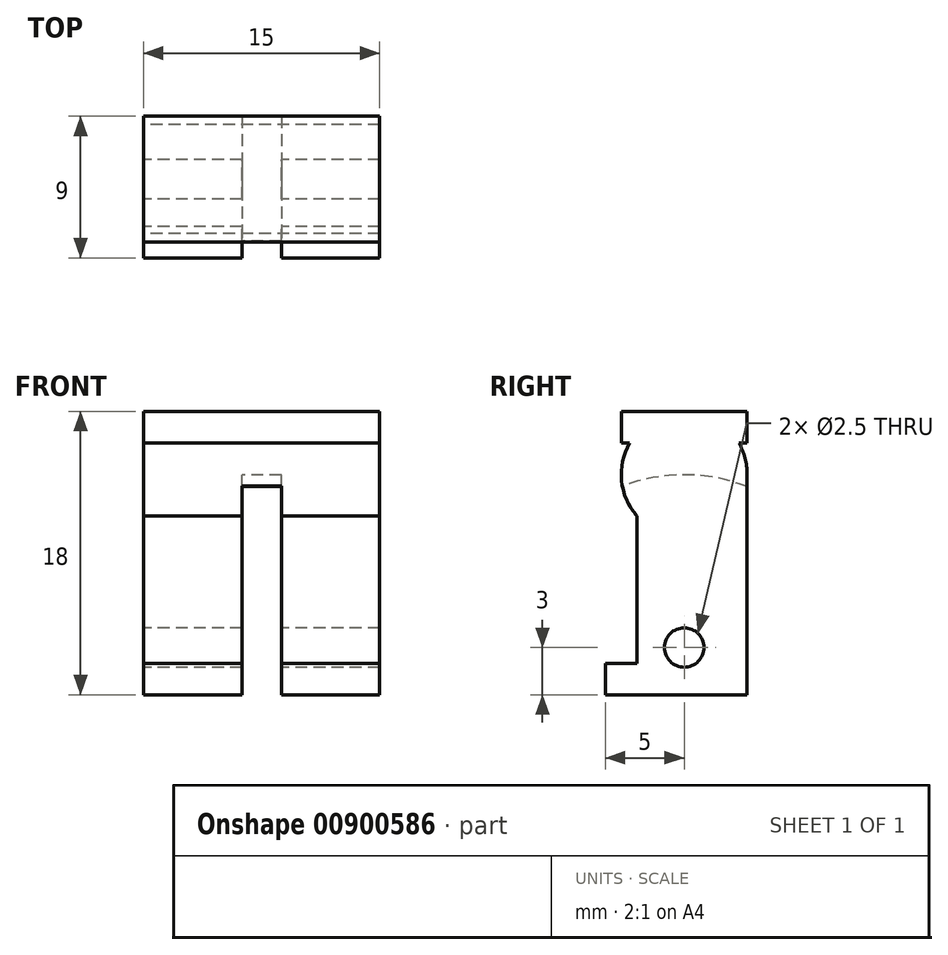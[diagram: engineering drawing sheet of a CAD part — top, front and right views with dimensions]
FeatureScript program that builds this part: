
annotation { "Feature Type Name" : "Feature", "Feature Type Description" : "" }
export const myFeature = defineFeature(function(context is Context, id is Id, definition is map)
    precondition{}
    {
        {
            var Q0;
            Q0=qCreatedBy(makeId("Right.planeOp"),FACE);
            var sketch = newSketch(context, id + "F0", { "sketchPlane" : qUnion([Q0])});
            skLineSegment(sketch, "E0.bottom", {"start": v(4, 1) * mm, "end": v(-4, 1) * mm});
            skLineSegment(sketch, "E0.top", {"start": v(4, -1) * mm, "end": v(3.46, -1) * mm});
            skLineSegment(sketch, "E0.left", {"start": v(4, 1) * mm, "end": v(4, -1) * mm});
            skLineSegment(sketch, "E0.right", {"start": v(-4, 1) * mm, "end": v(-4, -1) * mm});
            skPoint(sketch, "E0.middle", {"position": v(0, 0) * mm});
            skArc(sketch, "E1", {"start": v(-3.46, -1) * mm, "mid": v(-3.98, -3.4) * mm, "end": v(-3, -5.65) * mm});
            skLineSegment(sketch, "E2.left", {"start": v(4, -3) * mm, "end": v(4, -15) * mm});
            skLineSegment(sketch, "E2.right", {"start": v(-3, -5.65) * mm, "end": v(-3, -15) * mm});
            skLineSegment(sketch, "E3.bottom", {"start": v(0.75, -15) * mm, "end": v(-0.75, -15) * mm});
            skLineSegment(sketch, "E3.top", {"start": v(4, -17) * mm, "end": v(-5, -17) * mm});
            skLineSegment(sketch, "E3.left", {"start": v(4, -15) * mm, "end": v(4, -17) * mm});
            skLineSegment(sketch, "E3.right", {"start": v(-5, -15) * mm, "end": v(-5, -17) * mm});
            skCircle(sketch, "E4", {"center": v(0, -14) * mm, "radius": 1.25 * mm});
            skLineSegment(sketch, "E5.trimOffspring", {"start": v(-3.46, -1) * mm, "end": v(-4, -1) * mm});
            skArc(sketch, "E6.trimOffspring", {"start": v(4, -3) * mm, "mid": v(3.86, -1.96) * mm, "end": v(3.46, -1) * mm});
            skLineSegment(sketch, "E7.trimOffspring", {"start": v(-3, -15) * mm, "end": v(-5, -15) * mm});
            skSolve(sketch);
        }
        {
            var Q0;
            Q0 = qSketchRegion(id + "F0", true);
            extrude(context, id + "F1", {"entities" : qUnion([Q0]), "endBound" : BoundingType.SYMMETRIC, "depth" : 15 * mm, "offsetDistance" : 25 * mm});
        }
        {
            var Q0;
            Q0=qCreatedBy(makeId("Right.planeOp"),FACE);
            var sketch = newSketch(context, id + "F2", { "sketchPlane" : qUnion([Q0])});
            skCircle(sketch, "E8", {"center": v(0, -14.03) * mm, "radius": 11 * mm});
            skSolve(sketch);
        }
        {
            var Q0;
            Q0 = qSketchRegion(id + "F2", true);
            extrude(context, id + "F3", {"entities" : qUnion([Q0]), "operationType" : NewBodyOperationType.REMOVE, "endBound" : BoundingType.SYMMETRIC, "depth" : 2.5 * mm, "offsetDistance" : 25 * mm});
        }
    });
